# Revit family: DTI_A3-2032X1511-Square-Happy-Door
name_source: partatom
category: Doors
revit_build: Autodesk Revit 2016 (Build: 20150220_1215(x64)
units: mm (PartAtom-declared; Revit-internal decimal feet)

## family parameters
Always vertical = Yes
Cut with Voids When Loaded = No
Host = Wall
Room Calculation Point = No
Shared = No

## types (1)
- 2032 x 1511 Square - Happy Door
    Assembly Code = B2030130
    Frame Material = Kiln Dried Wood
    Frame Thickness = 85 mm  [stored 0.278871 ft]
    Frame Width = 55 mm  [stored 0.180446 ft]
    Function = Interior
    Glass Material = Glass
    Half = 701 mm
    Height = 2032 mm  [stored 6.66667 ft]
    Manufacturer = K. Parker Joinery
    Manufcturer Code = Square - Happy Door
    Model = Double
    Panel Height = 1977 mm
    Panel Width = 1401 mm
    URL = http://www.kparkerjoinery.co.za
    Wall Closure = By host
    Width = 1511 mm  [stored 4.95735 ft]

note: [stored X ft] marks values corroborated as IEEE doubles in the binary element streams (Revit-internal decimal feet)

## geometry (parser evidence)
native form markers: Sweep x13
no freeform markers — native parametric forms only
